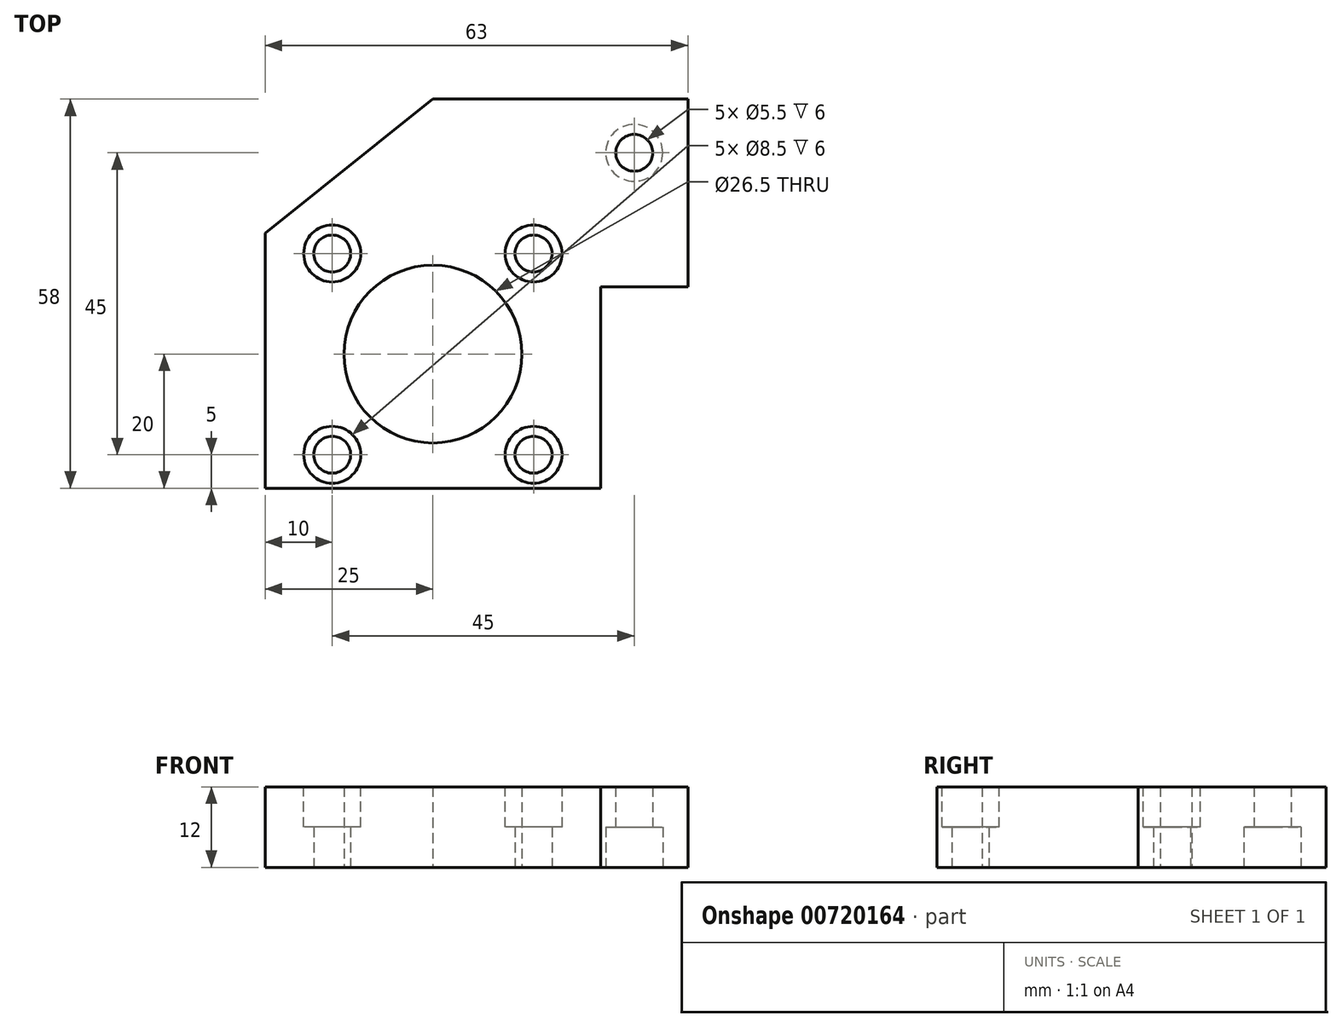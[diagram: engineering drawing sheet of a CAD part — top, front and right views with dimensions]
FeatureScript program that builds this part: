
annotation { "Feature Type Name" : "Feature", "Feature Type Description" : "" }
export const myFeature = defineFeature(function(context is Context, id is Id, definition is map)
    precondition{}
    {
        {
            var Q0;
            Q0=qCreatedBy(makeId("Top.planeOp"),FACE);
            var sketch = newSketch(context, id + "F0", { "sketchPlane" : qUnion([Q0])});
            skLineSegment(sketch, "E0", {"start": v(0, 0) * mm, "end": v(50, 0) * mm});
            skLineSegment(sketch, "E1", {"start": v(50, 0) * mm, "end": v(50, 30) * mm});
            skLineSegment(sketch, "E2", {"start": v(50, 30) * mm, "end": v(63, 30) * mm});
            skLineSegment(sketch, "E3", {"start": v(63, 30) * mm, "end": v(63, 58) * mm});
            skLineSegment(sketch, "E4", {"start": v(63, 58) * mm, "end": v(25, 58) * mm});
            skLineSegment(sketch, "E5", {"start": v(0, 0) * mm, "end": v(0, 38) * mm});
            skLineSegment(sketch, "E6", {"start": v(0, 38) * mm, "end": v(25, 58) * mm});
            skCircle(sketch, "E7", {"center": v(25, 20) * mm, "radius": 13.25 * mm});
            skCircle(sketch, "E8", {"center": v(10, 35) * mm, "radius": 2.75 * mm});
            skCircle(sketch, "E9", {"center": v(40, 35) * mm, "radius": 2.75 * mm});
            skCircle(sketch, "E10", {"center": v(10, 5) * mm, "radius": 2.75 * mm});
            skCircle(sketch, "E11", {"center": v(40, 5) * mm, "radius": 2.75 * mm});
            skCircle(sketch, "E12", {"center": v(55, 50) * mm, "radius": 2.75 * mm});
            skSolve(sketch);
        }
        {
            var Q0;
            Q0=makeQuery(id+"F0.imprint","IMPRINT",FACE,{"disambiguationData":[TD([[makeQuery(id+"F0.imprint","IMPRINT",EDGE,{"derivedFrom":sQuery(id+"F0.wireOp",EDGE,"E0")}),1.0]])]});
            extrude(context, id + "F1", {"entities" : qUnion([Q0]), "depth" : 12 * mm, "offsetDistance" : 25 * mm});
        }
        {
            var Q0;
            Q0=makeQuery(id+"F1.opExtrude","CAP_FACE",FACE,{"disambiguationData":[OSD([sQuery(id+"F0.wireOp",EDGE,"E0"),sQuery(id+"F0.wireOp",EDGE,"E1"),sQuery(id+"F0.wireOp",EDGE,"E2"),sQuery(id+"F0.wireOp",EDGE,"E3"),sQuery(id+"F0.wireOp",EDGE,"E4"),sQuery(id+"F0.wireOp",EDGE,"E5"),sQuery(id+"F0.wireOp",EDGE,"E6"),sQuery(id+"F0.wireOp",EDGE,"E7"),sQuery(id+"F0.wireOp",EDGE,"E8"),sQuery(id+"F0.wireOp",EDGE,"E9"),sQuery(id+"F0.wireOp",EDGE,"E10"),sQuery(id+"F0.wireOp",EDGE,"E11"),sQuery(id+"F0.wireOp",EDGE,"E12")])],"isStart":false});
            var sketch = newSketch(context, id + "F2", { "sketchPlane" : qUnion([Q0])});
            skCircle(sketch, "E13", {"center": v(10, 35) * mm, "radius": 4.25 * mm});
            skCircle(sketch, "E14", {"center": v(40, 35) * mm, "radius": 4.25 * mm});
            skCircle(sketch, "E15", {"center": v(10, 5) * mm, "radius": 4.25 * mm});
            skCircle(sketch, "E16", {"center": v(40, 5) * mm, "radius": 4.25 * mm});
            skSolve(sketch);
        }
        {
            var Q0;
            Q0 = qSketchRegion(id + "F2", true);
            extrude(context, id + "F3", {"entities" : qUnion([Q0]), "operationType" : NewBodyOperationType.REMOVE, "oppositeDirection" : true, "depth" : 6 * mm, "offsetDistance" : 25 * mm});
        }
        {
            var Q0;
            Q0=makeQuery(id+"F1.opExtrude","CAP_FACE",FACE,{"disambiguationData":[OSD([sQuery(id+"F0.wireOp",EDGE,"E0"),sQuery(id+"F0.wireOp",EDGE,"E1"),sQuery(id+"F0.wireOp",EDGE,"E2"),sQuery(id+"F0.wireOp",EDGE,"E3"),sQuery(id+"F0.wireOp",EDGE,"E4"),sQuery(id+"F0.wireOp",EDGE,"E5"),sQuery(id+"F0.wireOp",EDGE,"E6"),sQuery(id+"F0.wireOp",EDGE,"E7"),sQuery(id+"F0.wireOp",EDGE,"E8"),sQuery(id+"F0.wireOp",EDGE,"E9"),sQuery(id+"F0.wireOp",EDGE,"E10"),sQuery(id+"F0.wireOp",EDGE,"E11"),sQuery(id+"F0.wireOp",EDGE,"E12")])],"isStart":true});
            var sketch = newSketch(context, id + "F4", { "sketchPlane" : qUnion([Q0])});
            skCircle(sketch, "E17", {"center": v(55, -50) * mm, "radius": 4.25 * mm});
            skSolve(sketch);
        }
        {
            var Q0;
            Q0 = qSketchRegion(id + "F4", true);
            extrude(context, id + "F5", {"entities" : qUnion([Q0]), "operationType" : NewBodyOperationType.REMOVE, "oppositeDirection" : true, "depth" : 6 * mm, "offsetDistance" : 25 * mm});
        }
    });
